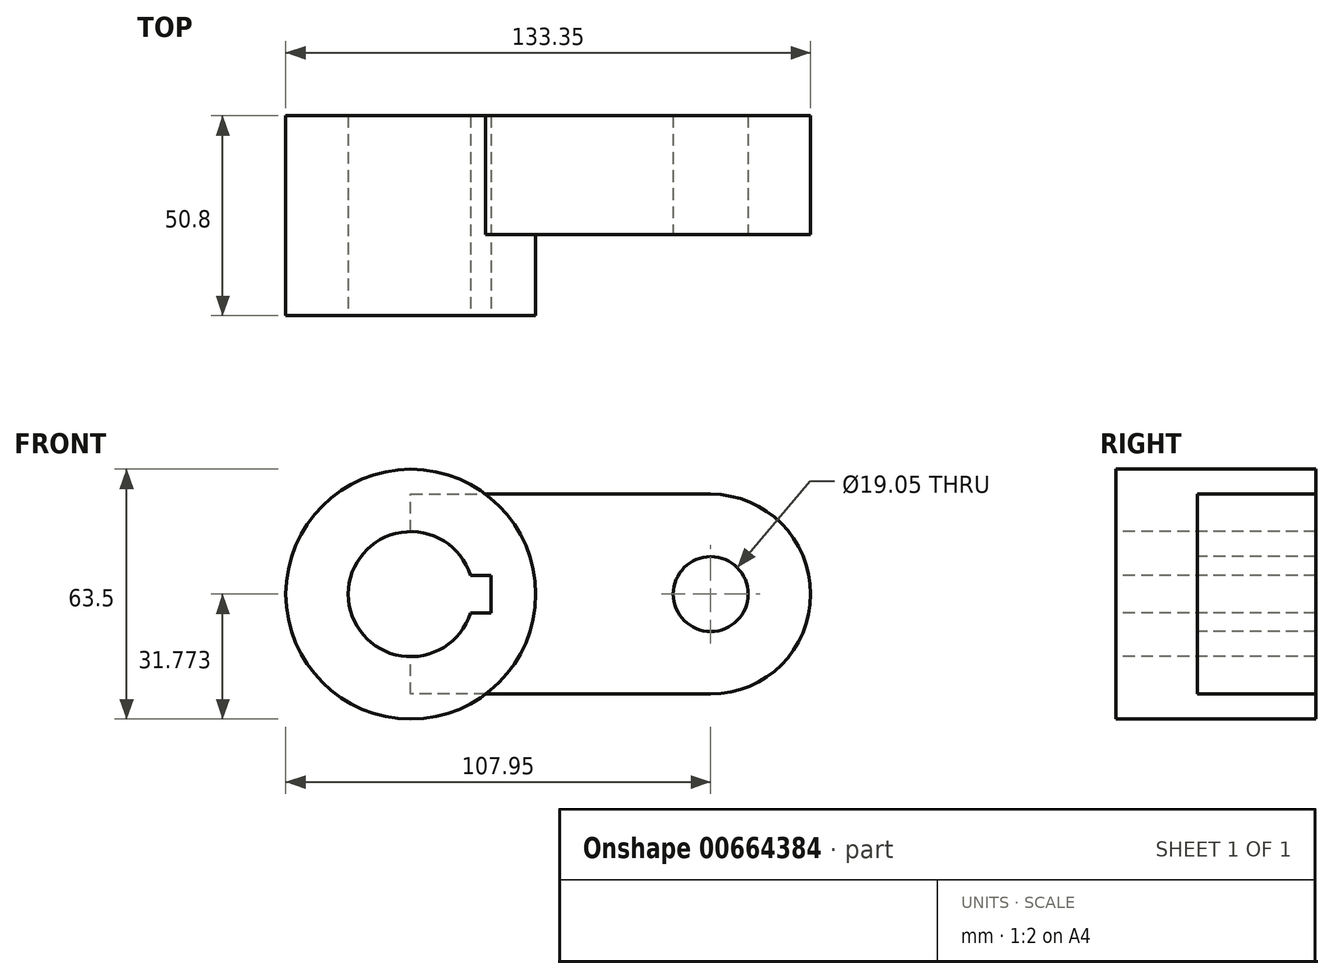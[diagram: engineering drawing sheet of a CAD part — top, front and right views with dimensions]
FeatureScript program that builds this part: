
annotation { "Feature Type Name" : "Feature", "Feature Type Description" : "" }
export const myFeature = defineFeature(function(context is Context, id is Id, definition is map)
    precondition{}
    {
        {
            var Q0;
            Q0=qCreatedBy(makeId("Front.planeOp"),FACE);
            var sketch = newSketch(context, id + "F0", { "sketchPlane" : qUnion([Q0])});
            skLineSegment(sketch, "E0", {"start": v(0, 0) * mm, "end": v(-76.2, 0) * mm});
            skLineSegment(sketch, "E1", {"start": v(-76.2, 0) * mm, "end": v(-76.2, 50.8) * mm});
            skLineSegment(sketch, "E2", {"start": v(-76.2, 50.8) * mm, "end": v(0, 50.8) * mm});
            skLineSegment(sketch, "E3", {"start": v(0, 50.8) * mm, "end": v(0, 0) * mm});
            skArc(sketch, "E4", {"start": v(0, 0) * mm, "mid": v(25.4, 25.4) * mm, "end": v(0, 50.8) * mm});
            skSolve(sketch);
        }
        {
            var Q0;
            Q0=makeQuery(id+"F0.imprint","IMPRINT",FACE,{"disambiguationData":[TD([[makeQuery(id+"F0.imprint","IMPRINT",EDGE,{"derivedFrom":sQuery(id+"F0.wireOp",EDGE,"E0")}),-1.0]])]});
            var Q1;
            Q1=makeQuery(id+"F0.imprint","IMPRINT",FACE,{"disambiguationData":[TD([[makeQuery(id+"F0.imprint","IMPRINT",EDGE,{"derivedFrom":sQuery(id+"F0.wireOp",EDGE,"E3")}),1.0]])]});
            extrude(context, id + "F1", {"entities" : qUnion([Q0, Q1]), "depth" : 30.16 * mm, "offsetDistance" : 25.4 * mm});
        }
        {
            var Q0;
            Q0=makeQuery(id+"F1.opExtrude","CAP_FACE",FACE,{"disambiguationData":[OSD([sQuery(id+"F0.wireOp",EDGE,"E0"),sQuery(id+"F0.wireOp",EDGE,"E1"),sQuery(id+"F0.wireOp",EDGE,"E2"),sQuery(id+"F0.wireOp",EDGE,"E4")])],"isStart":false});
            var sketch = newSketch(context, id + "F2", { "sketchPlane" : qUnion([Q0])});
            skCircle(sketch, "E5", {"center": v(-76.2, 25.4) * mm, "radius": 31.75 * mm});
            skSolve(sketch);
        }
        {
            var Q0;
            {var subQ5=makeQuery(id+"F1.opExtrude","CAP_EDGE",EDGE,{"disambiguationData":[OSD([sQuery(id+"F0.wireOp",EDGE,"E1")])],"isStart":false});Q0=makeQuery(id+"F2.imprint","IMPRINT",FACE,{"disambiguationData":[TD([[makeQuery(id+"F2.imprint","IMPRINT",EDGE,{"derivedFrom":subQ5}),1.0]])]});}
            extrude(context, id + "F3", {"entities" : qUnion([Q0]), "operationType" : NewBodyOperationType.ADD, "oppositeDirection" : true, "depth" : 30.18 * mm, "offsetDistance" : 25.4 * mm});
        }
        {
            var Q0;
            {var subQ5=makeQuery(id+"F1.opExtrude","CAP_EDGE",EDGE,{"disambiguationData":[OSD([sQuery(id+"F0.wireOp",EDGE,"E1")])],"isStart":false});Q0=makeQuery(id+"F2.imprint","IMPRINT",FACE,{"disambiguationData":[TD([[makeQuery(id+"F2.imprint","IMPRINT",EDGE,{"derivedFrom":subQ5}),1.0]])]});}
            extrude(context, id + "F4", {"entities" : qUnion([Q0]), "operationType" : NewBodyOperationType.ADD, "depth" : 20.62 * mm, "offsetDistance" : 25.4 * mm});
        }
        {
            var Q0;
            {var subQ5=makeQuery(id+"F1.opExtrude","CAP_EDGE",EDGE,{"disambiguationData":[OSD([sQuery(id+"F0.wireOp",EDGE,"E1")])],"isStart":false});Q0=makeQuery(id+"F2.imprint","IMPRINT",FACE,{"disambiguationData":[TD([[makeQuery(id+"F2.imprint","IMPRINT",EDGE,{"derivedFrom":subQ5}),-1.0]])]});}
            extrude(context, id + "F5", {"entities" : qUnion([Q0]), "operationType" : NewBodyOperationType.ADD, "depth" : 20.62 * mm, "offsetDistance" : 25.4 * mm});
        }
        {
            var Q0;
            {var subQ0=sQuery(id+"F2.wireOp",EDGE,"E5");var subQ1=sQuery(id+"F0.wireOp",EDGE,"E2");var subQ2=sQuery(id+"F0.wireOp",EDGE,"E1");var subQ3=sQuery(id+"F0.wireOp",EDGE,"E0");Q0=makeQuery(id+"F5.boolean.opBoolean","MERGE",FACE,{"derivedFrom":[makeQuery(id+"F4.opExtrude","CAP_FACE",FACE,{"disambiguationData":[OSD([subQ3,subQ2,subQ1,subQ0])],"isStart":false}),makeQuery(id+"F5.opExtrude","CAP_FACE",FACE,{"disambiguationData":[OSD([subQ3,subQ2,subQ1,subQ0])],"isStart":false})]});}
            var sketch = newSketch(context, id + "F6", { "sketchPlane" : qUnion([Q0])});
            skCircle(sketch, "E6", {"center": v(-76.2, 25.4) * mm, "radius": 15.88 * mm});
            skLineSegment(sketch, "E7", {"start": v(-76.2, 25.4) * mm, "end": v(-55.79, 25.4) * mm});
            skLineSegment(sketch, "E8", {"start": v(-55.79, 25.4) * mm, "end": v(-55.79, 30.16) * mm});
            skLineSegment(sketch, "E9", {"start": v(-55.79, 25.4) * mm, "end": v(-55.79, 20.64) * mm});
            skLineSegment(sketch, "E10", {"start": v(-55.79, 30.16) * mm, "end": v(-61.06, 30.16) * mm});
            skLineSegment(sketch, "E11", {"start": v(-55.79, 20.64) * mm, "end": v(-61.06, 20.64) * mm});
            skSolve(sketch);
        }
        {
            var Q0;
            {var subQ0=sQuery(id+"F6.wireOp",EDGE,"E6");var subQ1=makeQuery(id+"F6.imprint","INTERSECT",VERTEX,{"derivedFrom":[subQ0,sQuery(id+"F6.wireOp",EDGE,"E10")]});Q0=makeQuery(id+"F6.imprint","IMPRINT",FACE,{"disambiguationData":[TD([[makeQuery(id+"F6.imprint","IMPRINT",EDGE,{"disambiguationData":[TD([[subQ1,1.0]])],"derivedFrom":subQ0}),1.0]])]});}
            var Q1;
            {var subQ4=sQuery(id+"F6.wireOp",EDGE,"E8");Q1=makeQuery(id+"F6.imprint","IMPRINT",FACE,{"disambiguationData":[TD([[makeQuery(id+"F6.imprint","IMPRINT",EDGE,{"derivedFrom":subQ4}),1.0]])]});}
            var Q2;
            {var subQ4=sQuery(id+"F6.wireOp",EDGE,"E9");Q2=makeQuery(id+"F6.imprint","IMPRINT",FACE,{"disambiguationData":[TD([[makeQuery(id+"F6.imprint","IMPRINT",EDGE,{"derivedFrom":subQ4}),-1.0]])]});}
            extrude(context, id + "F7", {"entities" : qUnion([Q0, Q1, Q2]), "operationType" : NewBodyOperationType.REMOVE, "oppositeDirection" : true, "depth" : 50.8 * mm, "offsetDistance" : 25.4 * mm});
        }
        {
            var Q0;
            {var subQ5=makeQuery(id+"F1.opExtrude","CAP_EDGE",EDGE,{"disambiguationData":[OSD([sQuery(id+"F0.wireOp",EDGE,"E4")])],"isStart":false});Q0=makeQuery(id+"F2.imprint","IMPRINT",FACE,{"disambiguationData":[TD([[makeQuery(id+"F2.imprint","IMPRINT",EDGE,{"derivedFrom":subQ5}),1.0]])]});}
            var sketch = newSketch(context, id + "F8", { "sketchPlane" : qUnion([Q0])});
            skCircle(sketch, "E12", {"center": v(0, 25.42) * mm, "radius": 9.53 * mm});
            skSolve(sketch);
        }
        {
            var Q0;
            Q0=makeQuery(id+"F8.imprint","IMPRINT",FACE,{"disambiguationData":[TD([[makeQuery(id+"F8.imprint","IMPRINT",EDGE,{"derivedFrom":sQuery(id+"F8.wireOp",EDGE,"E12")}),1.0]])]});
            extrude(context, id + "F9", {"entities" : qUnion([Q0]), "operationType" : NewBodyOperationType.REMOVE, "oppositeDirection" : true, "depth" : 30.18 * mm, "offsetDistance" : 25.4 * mm});
        }
    });
